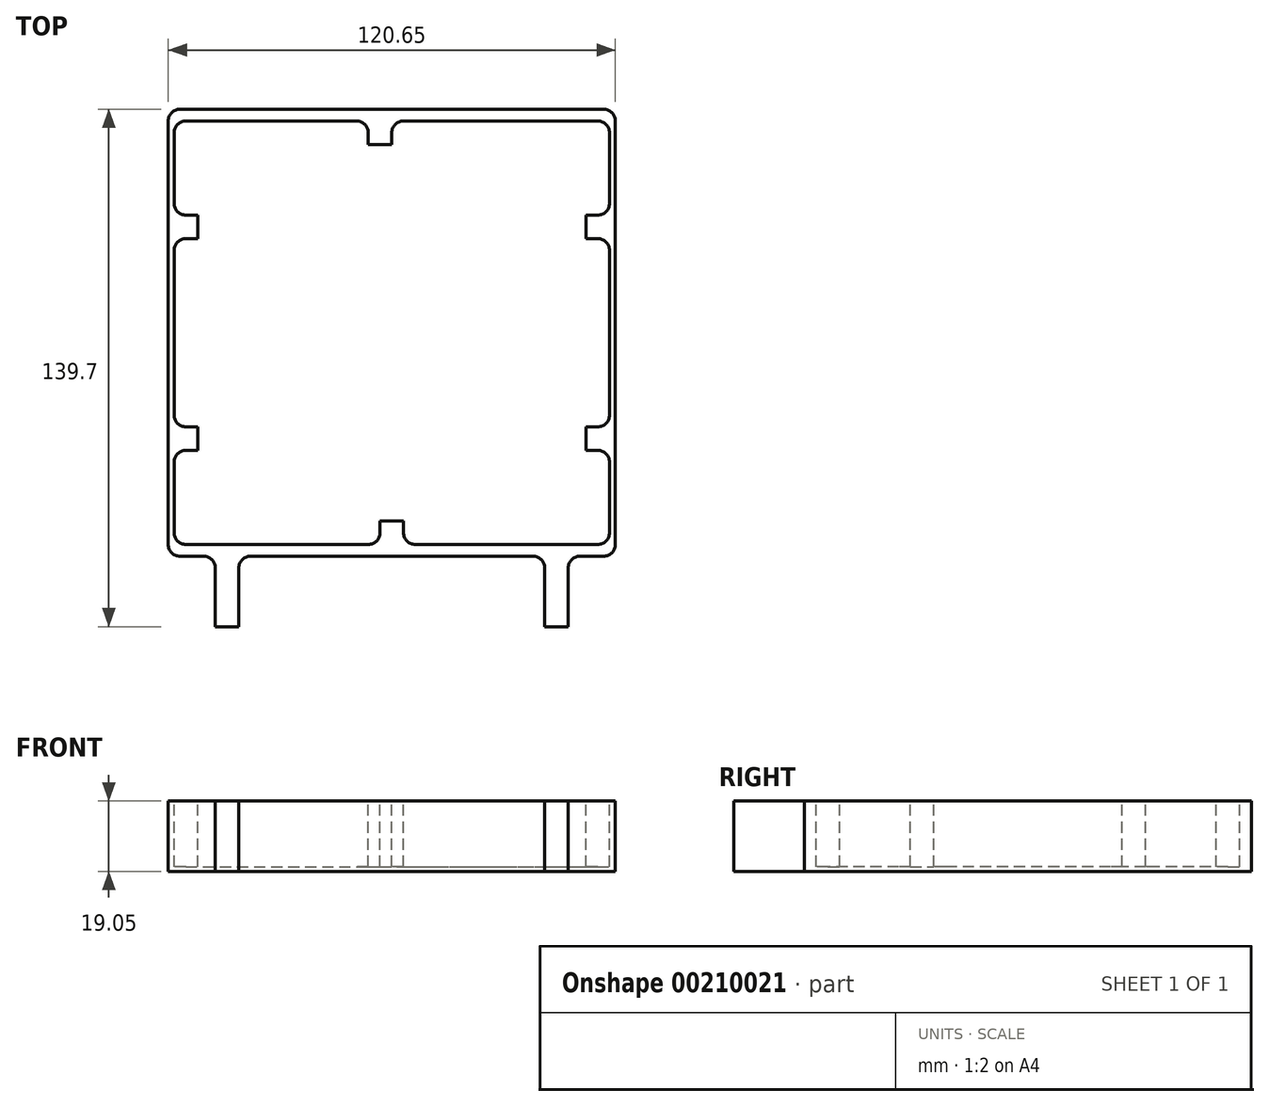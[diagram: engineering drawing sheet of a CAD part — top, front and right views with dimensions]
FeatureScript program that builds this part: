
annotation { "Feature Type Name" : "Feature", "Feature Type Description" : "" }
export const myFeature = defineFeature(function(context is Context, id is Id, definition is map)
    precondition{}
    {
        {
            var Q0;
            Q0=qCreatedBy(makeId("Top.planeOp"),FACE);
            var sketch = newSketch(context, id + "F0", { "sketchPlane" : qUnion([Q0])});
            skLineSegment(sketch, "E0.bottom", {"start": v(-54.6, 65.98) * mm, "end": v(59.7, 65.98) * mm});
            skLineSegment(sketch, "E0.top", {"start": v(-54.6, -54.67) * mm, "end": v(-48.25, -54.67) * mm});
            skLineSegment(sketch, "E0.left", {"start": v(-57.78, 62.8) * mm, "end": v(-57.78, -51.5) * mm});
            skLineSegment(sketch, "E0.right", {"start": v(62.87, 62.8) * mm, "end": v(62.87, -51.5) * mm});
            skPoint(sketch, "E1.visualSharp", {"position": v(-57.78, 65.98) * mm});
            skArc(sketch, "E1.filletArc", {"start": v(-54.6, 65.98) * mm, "mid": v(-56.85, 65.05) * mm, "end": v(-57.78, 62.8) * mm});
            skPoint(sketch, "E2.visualSharp", {"position": v(62.87, 65.98) * mm});
            skArc(sketch, "E2.filletArc", {"start": v(62.87, 62.8) * mm, "mid": v(61.94, 65.05) * mm, "end": v(59.7, 65.98) * mm});
            skPoint(sketch, "E3.visualSharp", {"position": v(62.87, -54.67) * mm});
            skArc(sketch, "E3.filletArc", {"start": v(59.7, -54.67) * mm, "mid": v(61.94, -53.74) * mm, "end": v(62.87, -51.5) * mm});
            skPoint(sketch, "E4.visualSharp", {"position": v(-57.78, -54.67) * mm});
            skArc(sketch, "E4.filletArc", {"start": v(-57.78, -51.5) * mm, "mid": v(-56.85, -53.74) * mm, "end": v(-54.6, -54.67) * mm});
            skLineSegment(sketch, "E5.top", {"start": v(-45.08, -73.72) * mm, "end": v(-38.73, -73.72) * mm});
            skLineSegment(sketch, "E5.left", {"start": v(-45.08, -57.85) * mm, "end": v(-45.08, -73.72) * mm});
            skLineSegment(sketch, "E5.right", {"start": v(-38.73, -57.85) * mm, "end": v(-38.73, -73.72) * mm});
            skLineSegment(sketch, "E6.top", {"start": v(50.17, -73.72) * mm, "end": v(43.82, -73.72) * mm});
            skLineSegment(sketch, "E6.left", {"start": v(50.17, -57.85) * mm, "end": v(50.17, -73.72) * mm});
            skLineSegment(sketch, "E6.right", {"start": v(43.82, -57.85) * mm, "end": v(43.82, -73.72) * mm});
            skLineSegment(sketch, "E7.trimOffspring", {"start": v(53.35, -54.67) * mm, "end": v(59.7, -54.67) * mm});
            skLineSegment(sketch, "E8.trimOffspring", {"start": v(-35.55, -54.67) * mm, "end": v(40.65, -54.67) * mm});
            skPoint(sketch, "E9.visualSharp", {"position": v(-38.73, -54.67) * mm});
            skArc(sketch, "E9.filletArc", {"start": v(-35.55, -54.67) * mm, "mid": v(-37.8, -55.6) * mm, "end": v(-38.73, -57.85) * mm});
            skPoint(sketch, "E10.visualSharp", {"position": v(-45.08, -54.67) * mm});
            skArc(sketch, "E10.filletArc", {"start": v(-45.08, -57.85) * mm, "mid": v(-46, -55.6) * mm, "end": v(-48.25, -54.67) * mm});
            skPoint(sketch, "E11.visualSharp", {"position": v(50.17, -54.67) * mm});
            skArc(sketch, "E11.filletArc", {"start": v(53.35, -54.67) * mm, "mid": v(51.1, -55.6) * mm, "end": v(50.17, -57.85) * mm});
            skPoint(sketch, "E12.visualSharp", {"position": v(43.82, -54.67) * mm});
            skArc(sketch, "E12.filletArc", {"start": v(43.82, -57.85) * mm, "mid": v(42.9, -55.6) * mm, "end": v(40.65, -54.67) * mm});
            skSolve(sketch);
        }
        {
            var Q0;
            Q0 = qSketchRegion(id + "F0", true);
            extrude(context, id + "F1", {"entities" : qUnion([Q0]), "depth" : 19.05 * mm});
        }
        {
            var Q0;
            Q0=makeQuery(id+"F1.opExtrude","CAP_FACE",FACE,{"disambiguationData":[OSD([sQuery(id+"F0.wireOp",EDGE,"E0.bottom"),sQuery(id+"F0.wireOp",EDGE,"E0.top"),sQuery(id+"F0.wireOp",EDGE,"E0.left"),sQuery(id+"F0.wireOp",EDGE,"E0.right"),sQuery(id+"F0.wireOp",EDGE,"E1.filletArc"),sQuery(id+"F0.wireOp",EDGE,"E2.filletArc"),sQuery(id+"F0.wireOp",EDGE,"E3.filletArc"),sQuery(id+"F0.wireOp",EDGE,"E4.filletArc"),sQuery(id+"F0.wireOp",EDGE,"E5.top"),sQuery(id+"F0.wireOp",EDGE,"E5.left"),sQuery(id+"F0.wireOp",EDGE,"E5.right"),sQuery(id+"F0.wireOp",EDGE,"E6.top"),sQuery(id+"F0.wireOp",EDGE,"E6.left"),sQuery(id+"F0.wireOp",EDGE,"E6.right"),sQuery(id+"F0.wireOp",EDGE,"E7.trimOffspring"),sQuery(id+"F0.wireOp",EDGE,"E8.trimOffspring"),sQuery(id+"F0.wireOp",EDGE,"E9.filletArc"),sQuery(id+"F0.wireOp",EDGE,"E10.filletArc"),sQuery(id+"F0.wireOp",EDGE,"E11.filletArc"),sQuery(id+"F0.wireOp",EDGE,"E12.filletArc")])],"isStart":false});
            var sketch = newSketch(context, id + "F2", { "sketchPlane" : qUnion([Q0])});
            skLineSegment(sketch, "E13.bottom", {"start": v(-53.01, 62.8) * mm, "end": v(-6.98, 62.8) * mm});
            skLineSegment(sketch, "E13.top", {"start": v(-53.01, -51.5) * mm, "end": v(-3.8, -51.5) * mm});
            skLineSegment(sketch, "E13.left", {"start": v(-56.19, 59.63) * mm, "end": v(-56.19, 40.58) * mm});
            skLineSegment(sketch, "E13.right", {"start": v(61.29, 59.63) * mm, "end": v(61.29, 40.58) * mm});
            skPoint(sketch, "E14.visualSharp", {"position": v(-56.19, 62.8) * mm});
            skArc(sketch, "E14.filletArc", {"start": v(-53.01, 62.8) * mm, "mid": v(-55.26, 61.87) * mm, "end": v(-56.19, 59.63) * mm});
            skPoint(sketch, "E15.visualSharp", {"position": v(61.29, 62.8) * mm});
            skArc(sketch, "E15.filletArc", {"start": v(61.29, 59.63) * mm, "mid": v(60.36, 61.87) * mm, "end": v(58.11, 62.8) * mm});
            skPoint(sketch, "E16.visualSharp", {"position": v(61.29, -51.5) * mm});
            skArc(sketch, "E16.filletArc", {"start": v(58.11, -51.5) * mm, "mid": v(60.36, -50.57) * mm, "end": v(61.29, -48.32) * mm});
            skPoint(sketch, "E17.visualSharp", {"position": v(-56.19, -51.5) * mm});
            skArc(sketch, "E17.filletArc", {"start": v(-56.19, -48.32) * mm, "mid": v(-55.26, -50.57) * mm, "end": v(-53.01, -51.5) * mm});
            skPoint(sketch, "E18.oppositeSnap0", {"position": v(2.55, 62.8) * mm});
            skLineSegment(sketch, "E18.top", {"start": v(-3.8, 56.45) * mm, "end": v(2.55, 56.45) * mm});
            skLineSegment(sketch, "E18.left", {"start": v(-3.8, 59.63) * mm, "end": v(-3.8, 56.45) * mm});
            skLineSegment(sketch, "E18.right", {"start": v(2.55, 59.63) * mm, "end": v(2.55, 56.45) * mm});
            skLineSegment(sketch, "E19.trimOffspring", {"start": v(5.72, 62.8) * mm, "end": v(58.11, 62.8) * mm});
            skLineSegment(sketch, "E20.top", {"start": v(-0.63, -45.15) * mm, "end": v(5.72, -45.15) * mm});
            skLineSegment(sketch, "E20.left", {"start": v(-0.63, -48.32) * mm, "end": v(-0.63, -45.15) * mm});
            skLineSegment(sketch, "E20.right", {"start": v(5.72, -48.32) * mm, "end": v(5.72, -45.15) * mm});
            skLineSegment(sketch, "E21.trimOffspring", {"start": v(8.9, -51.5) * mm, "end": v(58.11, -51.5) * mm});
            skLineSegment(sketch, "E22.bottom", {"start": v(-53.01, 37.4) * mm, "end": v(-49.84, 37.4) * mm});
            skLineSegment(sketch, "E22.top", {"start": v(-53.01, 31.05) * mm, "end": v(-49.84, 31.05) * mm});
            skLineSegment(sketch, "E22.right", {"start": v(-49.84, 37.4) * mm, "end": v(-49.84, 31.05) * mm});
            skLineSegment(sketch, "E23.bottom", {"start": v(-53.01, -26.1) * mm, "end": v(-49.84, -26.1) * mm});
            skLineSegment(sketch, "E23.top", {"start": v(-53.01, -19.75) * mm, "end": v(-49.84, -19.75) * mm});
            skLineSegment(sketch, "E23.right", {"start": v(-49.84, -26.1) * mm, "end": v(-49.84, -19.75) * mm});
            skLineSegment(sketch, "E24.bottom", {"start": v(58.11, 31.05) * mm, "end": v(54.94, 31.05) * mm});
            skLineSegment(sketch, "E24.top", {"start": v(58.11, 37.4) * mm, "end": v(54.94, 37.4) * mm});
            skLineSegment(sketch, "E24.right", {"start": v(54.94, 31.05) * mm, "end": v(54.94, 37.4) * mm});
            skPoint(sketch, "E25.firstSnap0", {"position": v(-53.01, -26.1) * mm});
            skLineSegment(sketch, "E25.bottom", {"start": v(58.11, -26.1) * mm, "end": v(54.94, -26.1) * mm});
            skLineSegment(sketch, "E25.top", {"start": v(58.11, -19.75) * mm, "end": v(54.94, -19.75) * mm});
            skLineSegment(sketch, "E25.right", {"start": v(54.94, -26.1) * mm, "end": v(54.94, -19.75) * mm});
            skLineSegment(sketch, "E26.trimOffspring", {"start": v(-56.19, -29.27) * mm, "end": v(-56.19, -48.32) * mm});
            skLineSegment(sketch, "E27.trimOffspring", {"start": v(61.29, -29.27) * mm, "end": v(61.29, -48.32) * mm});
            skLineSegment(sketch, "E28.trimOffspring", {"start": v(-56.19, 27.88) * mm, "end": v(-56.19, -16.57) * mm});
            skLineSegment(sketch, "E29.trimOffspring", {"start": v(61.29, 27.88) * mm, "end": v(61.29, -16.57) * mm});
            skPoint(sketch, "E30.visualSharp", {"position": v(-56.19, 37.4) * mm});
            skArc(sketch, "E30.filletArc", {"start": v(-56.19, 40.58) * mm, "mid": v(-55.26, 38.33) * mm, "end": v(-53.01, 37.4) * mm});
            skPoint(sketch, "E31.visualSharp", {"position": v(-56.19, 31.05) * mm});
            skArc(sketch, "E31.filletArc", {"start": v(-53.01, 31.05) * mm, "mid": v(-55.26, 30.12) * mm, "end": v(-56.19, 27.88) * mm});
            skPoint(sketch, "E32.visualSharp", {"position": v(-56.19, -19.75) * mm});
            skArc(sketch, "E32.filletArc", {"start": v(-56.19, -16.57) * mm, "mid": v(-55.26, -18.82) * mm, "end": v(-53.01, -19.75) * mm});
            skPoint(sketch, "E33.visualSharp", {"position": v(61.29, -26.1) * mm});
            skArc(sketch, "E33.filletArc", {"start": v(61.29, -29.27) * mm, "mid": v(60.36, -27.03) * mm, "end": v(58.11, -26.1) * mm});
            skPoint(sketch, "E34.visualSharp", {"position": v(61.29, -19.75) * mm});
            skArc(sketch, "E34.filletArc", {"start": v(58.11, -19.75) * mm, "mid": v(60.36, -18.82) * mm, "end": v(61.29, -16.57) * mm});
            skPoint(sketch, "E35.visualSharp", {"position": v(61.29, 31.05) * mm});
            skArc(sketch, "E35.filletArc", {"start": v(61.29, 27.88) * mm, "mid": v(60.36, 30.12) * mm, "end": v(58.11, 31.05) * mm});
            skPoint(sketch, "E36.visualSharp", {"position": v(61.29, 37.4) * mm});
            skArc(sketch, "E36.filletArc", {"start": v(58.11, 37.4) * mm, "mid": v(60.36, 38.33) * mm, "end": v(61.29, 40.58) * mm});
            skPoint(sketch, "E37.visualSharp", {"position": v(-56.19, -26.1) * mm});
            skArc(sketch, "E37.filletArc", {"start": v(-53.01, -26.1) * mm, "mid": v(-55.26, -27.03) * mm, "end": v(-56.19, -29.27) * mm});
            skPoint(sketch, "E38.visualSharp", {"position": v(-3.8, 62.8) * mm});
            skArc(sketch, "E38.filletArc", {"start": v(-3.8, 59.63) * mm, "mid": v(-4.73, 61.87) * mm, "end": v(-6.98, 62.8) * mm});
            skArc(sketch, "E39.filletArc", {"start": v(5.72, 62.8) * mm, "mid": v(3.48, 61.87) * mm, "end": v(2.55, 59.63) * mm});
            skPoint(sketch, "E40.visualSharp", {"position": v(-0.63, -51.5) * mm});
            skArc(sketch, "E40.filletArc", {"start": v(-3.8, -51.5) * mm, "mid": v(-1.56, -50.57) * mm, "end": v(-0.63, -48.32) * mm});
            skPoint(sketch, "E41.visualSharp", {"position": v(5.72, -51.5) * mm});
            skArc(sketch, "E41.filletArc", {"start": v(5.72, -48.32) * mm, "mid": v(6.65, -50.57) * mm, "end": v(8.9, -51.5) * mm});
            skSolve(sketch);
        }
        {
            var Q0;
            Q0 = qSketchRegion(id + "F2", true);
            extrude(context, id + "F3", {"entities" : qUnion([Q0]), "operationType" : NewBodyOperationType.REMOVE, "oppositeDirection" : true, "depth" : 17.78 * mm});
        }
    });
